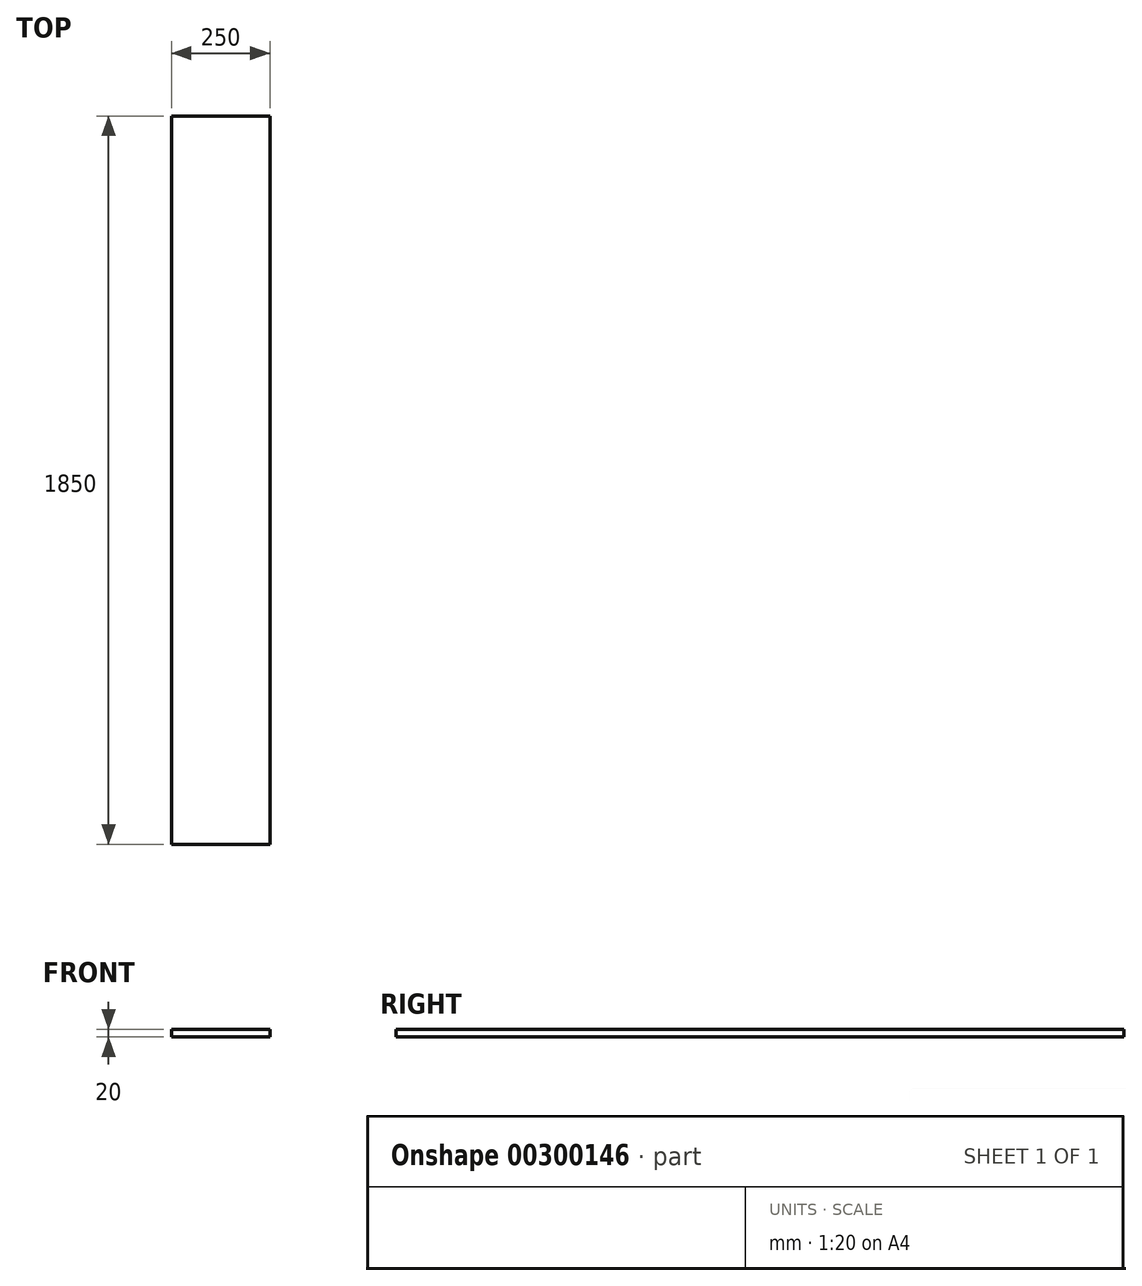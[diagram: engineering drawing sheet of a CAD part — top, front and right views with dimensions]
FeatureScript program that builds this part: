
annotation { "Feature Type Name" : "Feature", "Feature Type Description" : "" }
export const myFeature = defineFeature(function(context is Context, id is Id, definition is map)
    precondition{}
    {
        {
            var Q0;
            Q0=qCreatedBy(makeId("Top.planeOp"),FACE);
            var sketch = newSketch(context, id + "F0", { "sketchPlane" : qUnion([Q0])});
            skLineSegment(sketch, "E0.bottom", {"start": v(125, 925) * mm, "end": v(-125, 925) * mm});
            skLineSegment(sketch, "E0.top", {"start": v(125, -925) * mm, "end": v(-125, -925) * mm});
            skLineSegment(sketch, "E0.left", {"start": v(125, 925) * mm, "end": v(125, -925) * mm});
            skLineSegment(sketch, "E0.right", {"start": v(-125, 925) * mm, "end": v(-125, -925) * mm});
            skPoint(sketch, "E0.middle", {"position": v(0, 0) * mm});
            skSolve(sketch);
        }
        {
            var Q0;
            Q0=qSketchRegion(id+"F0",true);
            extrude(context, id + "F1", {"entities" : qUnion([Q0]), "endBound" : BoundingType.SYMMETRIC, "depth" : 20 * mm});
        }
    });
